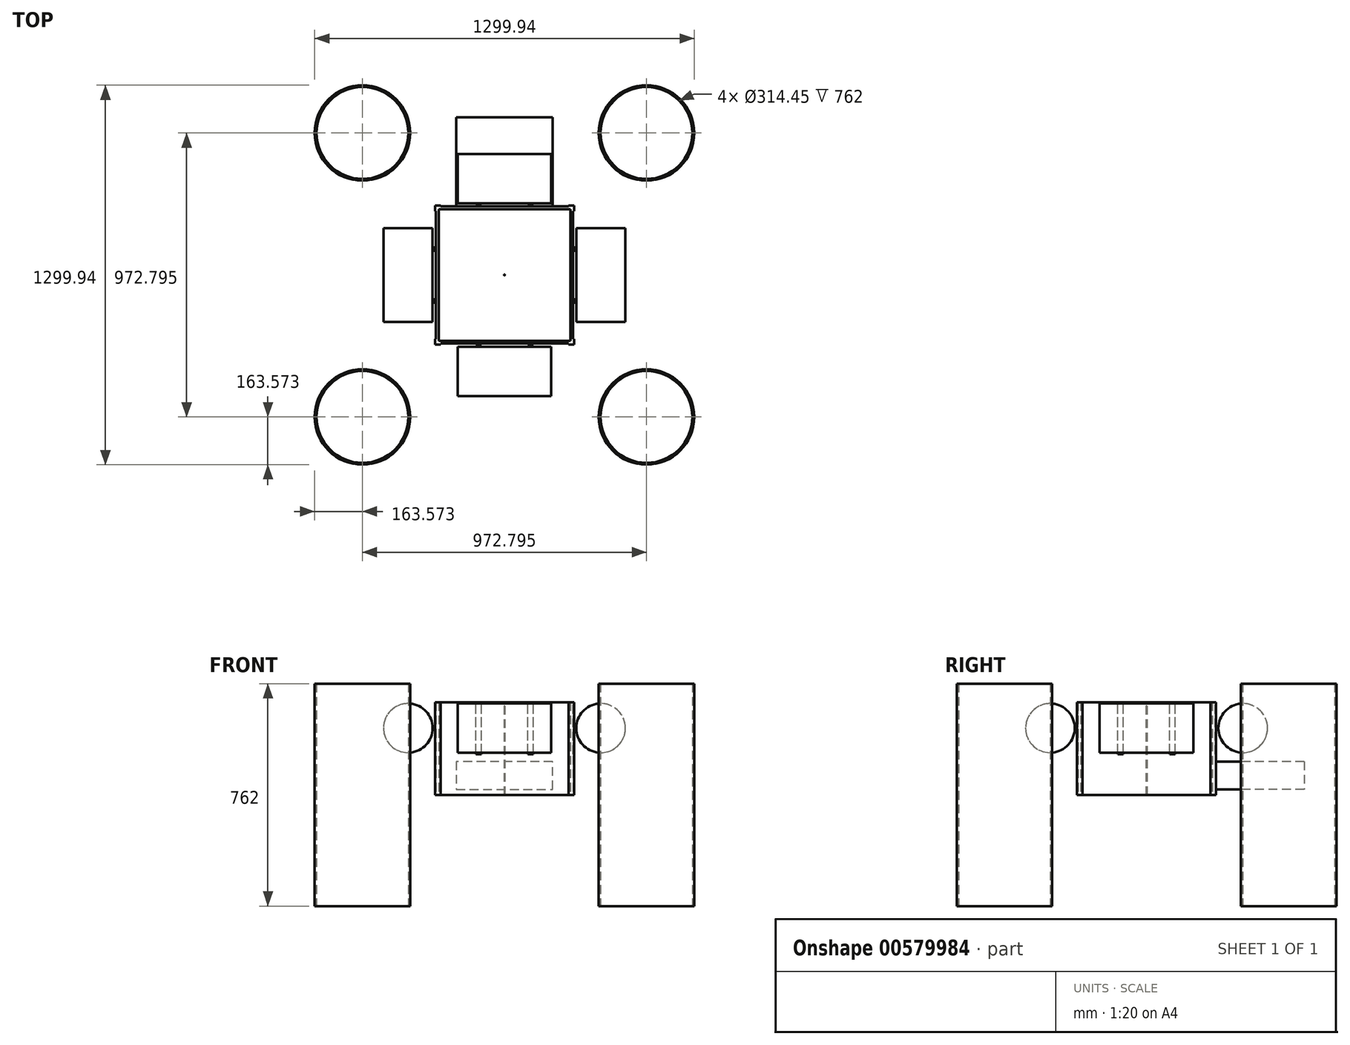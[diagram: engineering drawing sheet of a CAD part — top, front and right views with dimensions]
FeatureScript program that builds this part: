
annotation { "Feature Type Name" : "Feature", "Feature Type Description" : "" }
export const myFeature = defineFeature(function(context is Context, id is Id, definition is map)
    precondition{}
    {
        {
            var Q0;
            Q0=qCreatedBy(makeId("Top.planeOp"),FACE);
            var sketch = newSketch(context, id + "F0", { "sketchPlane" : qUnion([Q0])});
            skLineSegment(sketch, "E0.bottom", {"start": v(234.95, -234.95) * mm, "end": v(-234.95, -234.95) * mm});
            skLineSegment(sketch, "E0.top", {"start": v(234.95, 234.95) * mm, "end": v(-234.95, 234.95) * mm});
            skLineSegment(sketch, "E0.left", {"start": v(234.95, -234.95) * mm, "end": v(234.95, 234.95) * mm});
            skLineSegment(sketch, "E0.right", {"start": v(-234.95, -234.95) * mm, "end": v(-234.95, 234.95) * mm});
            skPoint(sketch, "E0.middle", {"position": v(0, 0) * mm});
            skLineSegment(sketch, "E1", {"start": v(-234.95, 238.13) * mm, "end": v(-238.13, 238.13) * mm});
            skLineSegment(sketch, "E2.bottom", {"start": v(-238.13, 238.13) * mm, "end": v(-219.08, 238.13) * mm});
            skLineSegment(sketch, "E2.top", {"start": v(-234.95, 234.95) * mm, "end": v(-219.08, 234.95) * mm});
            skLineSegment(sketch, "E2.left", {"start": v(-238.13, 238.13) * mm, "end": v(-238.13, 234.95) * mm});
            skLineSegment(sketch, "E2.right", {"start": v(-219.08, 238.13) * mm, "end": v(-219.08, 234.95) * mm});
            skLineSegment(sketch, "E3.bottom", {"start": v(-238.13, 238.13) * mm, "end": v(-234.95, 238.13) * mm});
            skLineSegment(sketch, "E3.top", {"start": v(-238.13, 219.08) * mm, "end": v(-234.95, 219.08) * mm});
            skLineSegment(sketch, "E3.left", {"start": v(-238.13, 238.13) * mm, "end": v(-238.13, 219.08) * mm});
            skLineSegment(sketch, "E3.right", {"start": v(-234.95, 234.95) * mm, "end": v(-234.95, 219.08) * mm});
            skLineSegment(sketch, "E4.1.0", {"start": v(-234.95, -234.95) * mm, "end": v(-219.08, -234.95) * mm});
            skLineSegment(sketch, "E4.1.1", {"start": v(-238.13, -238.13) * mm, "end": v(-219.08, -238.13) * mm});
            skLineSegment(sketch, "E4.1.2", {"start": v(-238.13, -238.13) * mm, "end": v(-238.13, -219.08) * mm});
            skLineSegment(sketch, "E4.1.3", {"start": v(-234.95, -234.95) * mm, "end": v(-234.95, -219.08) * mm});
            skLineSegment(sketch, "E4.1.4", {"start": v(-238.13, -219.08) * mm, "end": v(-234.95, -219.08) * mm});
            skLineSegment(sketch, "E4.1.5", {"start": v(-219.08, -238.13) * mm, "end": v(-219.08, -234.95) * mm});
            skLineSegment(sketch, "E4.1.6", {"start": v(-238.13, -238.13) * mm, "end": v(-234.95, -238.13) * mm});
            skLineSegment(sketch, "E4.1.7", {"start": v(-238.13, -238.13) * mm, "end": v(-238.13, -234.95) * mm});
            skLineSegment(sketch, "E4.1.8", {"start": v(-238.13, -234.95) * mm, "end": v(-238.13, -238.13) * mm});
            skLineSegment(sketch, "E4.2.0", {"start": v(234.95, -234.95) * mm, "end": v(234.95, -219.08) * mm});
            skLineSegment(sketch, "E4.2.1", {"start": v(238.13, -238.13) * mm, "end": v(238.13, -219.08) * mm});
            skLineSegment(sketch, "E4.2.2", {"start": v(238.13, -238.13) * mm, "end": v(219.08, -238.13) * mm});
            skLineSegment(sketch, "E4.2.3", {"start": v(234.95, -234.95) * mm, "end": v(219.08, -234.95) * mm});
            skLineSegment(sketch, "E4.2.4", {"start": v(219.08, -238.13) * mm, "end": v(219.08, -234.95) * mm});
            skLineSegment(sketch, "E4.2.5", {"start": v(238.13, -219.08) * mm, "end": v(234.95, -219.08) * mm});
            skLineSegment(sketch, "E4.2.6", {"start": v(238.13, -238.13) * mm, "end": v(238.13, -234.95) * mm});
            skLineSegment(sketch, "E4.2.7", {"start": v(238.13, -238.13) * mm, "end": v(234.95, -238.13) * mm});
            skLineSegment(sketch, "E4.2.8", {"start": v(234.95, -238.13) * mm, "end": v(238.13, -238.13) * mm});
            skLineSegment(sketch, "E4.3.0", {"start": v(234.95, 234.95) * mm, "end": v(219.08, 234.95) * mm});
            skLineSegment(sketch, "E4.3.1", {"start": v(238.13, 238.13) * mm, "end": v(219.08, 238.13) * mm});
            skLineSegment(sketch, "E4.3.2", {"start": v(238.13, 238.13) * mm, "end": v(238.13, 219.08) * mm});
            skLineSegment(sketch, "E4.3.3", {"start": v(234.95, 234.95) * mm, "end": v(234.95, 219.08) * mm});
            skLineSegment(sketch, "E4.3.4", {"start": v(238.13, 219.08) * mm, "end": v(234.95, 219.08) * mm});
            skLineSegment(sketch, "E4.3.5", {"start": v(219.08, 238.13) * mm, "end": v(219.08, 234.95) * mm});
            skLineSegment(sketch, "E4.3.6", {"start": v(238.13, 238.13) * mm, "end": v(234.95, 238.13) * mm});
            skLineSegment(sketch, "E4.3.7", {"start": v(238.13, 238.13) * mm, "end": v(238.13, 234.95) * mm});
            skLineSegment(sketch, "E4.3.8", {"start": v(238.13, 234.95) * mm, "end": v(238.13, 238.13) * mm});
            skLineSegment(sketch, "E5.0", {"start": v(225.43, 225.43) * mm, "end": v(-225.42, 225.42) * mm});
            skLineSegment(sketch, "E5.1", {"start": v(225.43, -225.42) * mm, "end": v(225.43, 225.42) * mm});
            skLineSegment(sketch, "E5.2", {"start": v(225.43, -225.42) * mm, "end": v(-225.42, -225.43) * mm});
            skLineSegment(sketch, "E5.3", {"start": v(-225.42, -225.43) * mm, "end": v(-225.42, 225.42) * mm});
            skSolve(sketch);
        }
        {
            var Q0;
            Q0=qSketchRegion(id+"F0",true);
            extrude(context, id + "F1", {"entities" : qUnion([Q0]), "depth" : 317.5 * mm, "offsetDistance" : 25.4 * mm});
        }
        {
            var Q0;
            Q0=qCreatedBy(makeId("Right.planeOp"),FACE);
            var sketch = newSketch(context, id + "F2", { "sketchPlane" : qUnion([Q0])});
            skLineSegment(sketch, "E6", {"start": v(234.95, 0) * mm, "end": v(234.95, 228.6) * mm});
            skLineSegment(sketch, "E7", {"start": v(234.95, 228.6) * mm, "end": v(330.2, 228.6) * mm});
            skCircle(sketch, "E8", {"center": v(330.2, 228.6) * mm, "radius": 84.14 * mm});
            skSolve(sketch);
        }
        {
            var Q0;
            Q0=qSketchRegion(id+"F2",true);
            extrude(context, id + "F3", {"entities" : qUnion([Q0]), "endBound" : BoundingType.SYMMETRIC, "depth" : 320.67 * mm, "offsetDistance" : 25.4 * mm});
        }
        {
            var Q0;
            Q0=makeQuery(id+"F1.opExtrude","CAP_FACE",FACE,{"disambiguationData":[OSD([sQuery(id+"F0.wireOp",EDGE,"E0.bottom"),sQuery(id+"F0.wireOp",EDGE,"E0.top"),sQuery(id+"F0.wireOp",EDGE,"E0.left"),sQuery(id+"F0.wireOp",EDGE,"E0.right"),sQuery(id+"F0.wireOp",EDGE,"E2.bottom"),sQuery(id+"F0.wireOp",EDGE,"E2.right"),sQuery(id+"F0.wireOp",EDGE,"E3.bottom"),sQuery(id+"F0.wireOp",EDGE,"E3.top"),sQuery(id+"F0.wireOp",EDGE,"E3.left"),sQuery(id+"F0.wireOp",EDGE,"E4.1.1"),sQuery(id+"F0.wireOp",EDGE,"E4.1.2"),sQuery(id+"F0.wireOp",EDGE,"E4.1.4"),sQuery(id+"F0.wireOp",EDGE,"E4.1.5"),sQuery(id+"F0.wireOp",EDGE,"E4.1.6"),sQuery(id+"F0.wireOp",EDGE,"E4.1.8"),sQuery(id+"F0.wireOp",EDGE,"E4.2.1"),sQuery(id+"F0.wireOp",EDGE,"E4.2.2"),sQuery(id+"F0.wireOp",EDGE,"E4.2.4"),sQuery(id+"F0.wireOp",EDGE,"E4.2.5"),sQuery(id+"F0.wireOp",EDGE,"E4.2.6"),sQuery(id+"F0.wireOp",EDGE,"E4.2.8"),sQuery(id+"F0.wireOp",EDGE,"E4.3.1"),sQuery(id+"F0.wireOp",EDGE,"E4.3.2"),sQuery(id+"F0.wireOp",EDGE,"E4.3.4"),sQuery(id+"F0.wireOp",EDGE,"E4.3.5"),sQuery(id+"F0.wireOp",EDGE,"E4.3.6"),sQuery(id+"F0.wireOp",EDGE,"E4.3.8"),sQuery(id+"F0.wireOp",EDGE,"E5.0"),sQuery(id+"F0.wireOp",EDGE,"E5.1"),sQuery(id+"F0.wireOp",EDGE,"E5.2"),sQuery(id+"F0.wireOp",EDGE,"E5.3")])],"isStart":false});
            var sketch = newSketch(context, id + "F4", { "sketchPlane" : qUnion([Q0])});
            skLineSegment(sketch, "E9", {"start": v(0, 234.95) * mm, "end": v(-79.38, 234.95) * mm});
            skLineSegment(sketch, "E10", {"start": v(-79.38, 234.95) * mm, "end": v(-79.38, 238.12) * mm});
            skLineSegment(sketch, "E11", {"start": v(-79.38, 238.12) * mm, "end": v(-98.43, 238.12) * mm});
            skLineSegment(sketch, "E12", {"start": v(-98.43, 238.12) * mm, "end": v(-98.43, 234.95) * mm});
            skLineSegment(sketch, "E13", {"start": v(-98.43, 234.95) * mm, "end": v(-79.38, 234.95) * mm});
            skLineSegment(sketch, "E14", {"start": v(0, 234.95) * mm, "end": v(0, 171.04) * mm});
            skPoint(sketch, "E14.endSnap0", {"position": v(0, 225.42) * mm});
            skLineSegment(sketch, "E15.MirrorCS", {"start": v(79.37, 234.95) * mm, "end": v(79.37, 238.12) * mm});
            skLineSegment(sketch, "E16.MirrorCS", {"start": v(98.43, 238.12) * mm, "end": v(98.43, 234.95) * mm});
            skLineSegment(sketch, "E17.MirrorCS", {"start": v(0, 234.95) * mm, "end": v(79.38, 234.95) * mm});
            skLineSegment(sketch, "E18.MirrorCS", {"start": v(79.38, 238.13) * mm, "end": v(98.43, 238.13) * mm});
            skLineSegment(sketch, "E19.MirrorCS", {"start": v(98.43, 234.95) * mm, "end": v(79.38, 234.95) * mm});
            skSolve(sketch);
        }
        {
            var Q0;
            Q0=qSketchRegion(id+"F4",true);
            extrude(context, id + "F5", {"entities" : qUnion([Q0]), "oppositeDirection" : true, "depth" : 177.8 * mm, "offsetDistance" : 25.4 * mm});
        }
        {
            var Q0;
            Q0=qCreatedBy(makeId("Top.planeOp"),FACE);
            var sketch = newSketch(context, id + "F6", { "sketchPlane" : qUnion([Q0])});
            skCircle(sketch, "E20", {"center": v(0, 0) * mm, "radius": 1.59 * mm});
            skSolve(sketch);
        }
        {
            var Q0;
            Q0=qSketchRegion(id+"F6",true);
            extrude(context, id + "F7", {"entities" : qUnion([Q0]), "depth" : 304.8 * mm, "offsetDistance" : 25.4 * mm});
        }
        {
            var Q0;
            Q0=makeQuery(id+"F3.opExtrude","SWEPT_BODY",BODY,{"disambiguationData":[OSD([sQuery(id+"F2.wireOp",EDGE,"E8")])]});
            var Q1;
            Q1=makeQuery(id+"F5.opExtrude","SWEPT_BODY",BODY,{"disambiguationData":[OSD([sQuery(id+"F4.wireOp",EDGE,"E10"),sQuery(id+"F4.wireOp",EDGE,"E11"),sQuery(id+"F4.wireOp",EDGE,"E12"),sQuery(id+"F4.wireOp",EDGE,"E13")])]});
            var Q2;
            Q2=makeQuery(id+"F5.opExtrude","SWEPT_BODY",BODY,{"disambiguationData":[OSD([sQuery(id+"F4.wireOp",EDGE,"E15.MirrorCS"),sQuery(id+"F4.wireOp",EDGE,"E16.MirrorCS"),sQuery(id+"F4.wireOp",EDGE,"E18.MirrorCS"),sQuery(id+"F4.wireOp",EDGE,"E19.MirrorCS")])]});
            var Q3;
            Q3=makeQuery(id+"F7.opExtrude","SWEPT_FACE",FACE,{"disambiguationData":[OSD([sQuery(id+"F6.wireOp",EDGE,"E20")])]});
            circularPattern(context, id + "F8", {"entities" : qUnion([Q0, Q1, Q2]), "axis" : qUnion([Q3]), "angle" : 360 * degree, "instanceCount" : 4, "equalSpace" : true});
        }
        {
            var Q0;
            Q0=makeQuery(id+"F1.opExtrude","SWEPT_FACE",FACE,{"disambiguationData":[OSD([sQuery(id+"F0.wireOp",EDGE,"E0.top")])]});
            var sketch = newSketch(context, id + "F9", { "sketchPlane" : qUnion([Q0])});
            skLineSegment(sketch, "E21", {"start": v(0, 0) * mm, "end": v(0, 19.05) * mm});
            skPoint(sketch, "E21.endSnap0", {"position": v(0, 0) * mm});
            skLineSegment(sketch, "E22", {"start": v(0, 19.05) * mm, "end": v(165.1, 19.05) * mm});
            skLineSegment(sketch, "E23.MirrorCS", {"start": v(0, 19.05) * mm, "end": v(-165.1, 19.05) * mm});
            skLineSegment(sketch, "E24", {"start": v(-165.1, 19.05) * mm, "end": v(-165.1, 114.3) * mm});
            skLineSegment(sketch, "E25", {"start": v(-165.1, 114.3) * mm, "end": v(165.1, 114.3) * mm});
            skLineSegment(sketch, "E26", {"start": v(165.1, 114.3) * mm, "end": v(165.1, 19.05) * mm});
            skSolve(sketch);
        }
        {
            var Q0;
            Q0=qSketchRegion(id+"F9",true);
            extrude(context, id + "F10", {"entities" : qUnion([Q0]), "depth" : 304.8 * mm, "offsetDistance" : 25.4 * mm});
        }
        {
            var Q0;
            Q0=makeQuery(id+"F1.opExtrude","SWEPT_FACE",FACE,{"disambiguationData":[OSD([sQuery(id+"F0.wireOp",EDGE,"E4.3.2"),sQuery(id+"F0.wireOp",EDGE,"E4.3.8")])]});
            var sketch = newSketch(context, id + "F11", { "sketchPlane" : qUnion([Q0])});
            skLineSegment(sketch, "E27", {"start": v(644.53, 0) * mm, "end": v(644.53, 25.4) * mm});
            skLineSegment(sketch, "E28", {"start": v(238.13, 317.5) * mm, "end": v(314.33, 317.5) * mm});
            skArc(sketch, "E29", {"start": v(640.07, 52.43) * mm, "mid": v(524.3, 242.86) * mm, "end": v(314.33, 317.5) * mm});
            skLineSegment(sketch, "E30", {"start": v(238.13, 0) * mm, "end": v(238.13, -1.27) * mm});
            skLineSegment(sketch, "E31", {"start": v(238.13, -1.27) * mm, "end": v(219.08, -1.27) * mm});
            skArc(sketch, "E32", {"start": v(238.12, -1.27) * mm, "mid": v(428.57, 4.57) * mm, "end": v(618.3, 22.06) * mm});
            skLineSegment(sketch, "E33", {"start": v(219.08, -1.27) * mm, "end": v(219.08, 0) * mm});
            skLineSegment(sketch, "E34", {"start": v(219.08, 0) * mm, "end": v(238.13, 0) * mm});
            skLineSegment(sketch, "E35", {"start": v(238.13, 317.5) * mm, "end": v(238.13, 292.1) * mm});
            skLineSegment(sketch, "E36", {"start": v(238.13, 317.5) * mm, "end": v(263.53, 317.5) * mm});
            skLineSegment(sketch, "E37", {"start": v(238.13, 292.1) * mm, "end": v(238.13, 266.7) * mm});
            skPoint(sketch, "E38.visualSharp", {"position": v(644.52, 25.4) * mm});
            skArc(sketch, "E38.filletArc", {"start": v(618.3, 22.06) * mm, "mid": v(635.84, 32.47) * mm, "end": v(640.07, 52.43) * mm});
            skArc(sketch, "E39.0", {"start": v(238.12, 0) * mm, "mid": v(428.5, 5.83) * mm, "end": v(618.15, 23.32) * mm});
            skArc(sketch, "E39.1", {"start": v(618.15, 23.32) * mm, "mid": v(634.81, 33.21) * mm, "end": v(638.82, 52.17) * mm});
            skArc(sketch, "E39.2", {"start": v(638.82, 52.17) * mm, "mid": v(523.5, 241.87) * mm, "end": v(314.33, 316.23) * mm});
            skLineSegment(sketch, "E39.3", {"start": v(238.13, 316.23) * mm, "end": v(314.33, 316.23) * mm});
            skLineSegment(sketch, "E40", {"start": v(263.53, 317.5) * mm, "end": v(263.53, 316.23) * mm});
            skArc(sketch, "E41", {"start": v(263.53, 316.23) * mm, "mid": v(245.65, 309.62) * mm, "end": v(238.13, 292.1) * mm});
            skLineSegment(sketch, "E42", {"start": v(263.53, 316.23) * mm, "end": v(288.93, 316.23) * mm});
            skLineSegment(sketch, "E43.0", {"start": v(263.5, 314.96) * mm, "end": v(288.93, 314.96) * mm});
            skArc(sketch, "E43.1", {"start": v(263.5, 314.96) * mm, "mid": v(246.53, 308.7) * mm, "end": v(239.4, 292.1) * mm});
            skLineSegment(sketch, "E43.2", {"start": v(239.4, 292.1) * mm, "end": v(239.4, 266.7) * mm});
            skLineSegment(sketch, "E44", {"start": v(288.93, 314.96) * mm, "end": v(288.93, 316.23) * mm});
            skLineSegment(sketch, "E45", {"start": v(238.13, 266.7) * mm, "end": v(239.4, 266.7) * mm});
            skLineSegment(sketch, "E46", {"start": v(238.13, 317.5) * mm, "end": v(234.95, 317.5) * mm});
            skLineSegment(sketch, "E47", {"start": v(234.95, 317.5) * mm, "end": v(234.95, 316.23) * mm});
            skLineSegment(sketch, "E48", {"start": v(234.95, 316.23) * mm, "end": v(238.13, 316.23) * mm});
            skSolve(sketch);
        }
        {
            var Q0;
            Q0=qSketchRegion(id+"F11",true);
            extrude(context, id + "F12", {"entities" : qUnion([Q0]), "oppositeDirection" : true, "depth" : 679.45 * mm, "offsetDistance" : 25.4 * mm, "hasSecondDirection" : true, "secondDirectionOppositeDirection" : false, "secondDirectionDepth" : 203.2 * mm});
        }
        {
            var Q0;
            Q0=qCreatedBy(makeId("Top.planeOp"),FACE);
            var sketch = newSketch(context, id + "F13", { "sketchPlane" : qUnion([Q0])});
            skLineSegment(sketch, "E49", {"start": v(0, 0) * mm, "end": v(0, 486.4) * mm});
            skLineSegment(sketch, "E50", {"start": v(0, 486.4) * mm, "end": v(486.4, 486.4) * mm});
            skCircle(sketch, "E51", {"center": v(486.4, 486.4) * mm, "radius": 157.23 * mm});
            skCircle(sketch, "E52.0", {"center": v(486.4, 486.4) * mm, "radius": 163.58 * mm});
            skCircle(sketch, "E53.1.0", {"center": v(-486.4, 486.4) * mm, "radius": 163.58 * mm});
            skCircle(sketch, "E53.1.1", {"center": v(-486.4, 486.4) * mm, "radius": 157.23 * mm});
            skCircle(sketch, "E53.2.0", {"center": v(-486.4, -486.4) * mm, "radius": 163.58 * mm});
            skCircle(sketch, "E53.2.1", {"center": v(-486.4, -486.4) * mm, "radius": 157.23 * mm});
            skCircle(sketch, "E53.3.0", {"center": v(486.4, -486.4) * mm, "radius": 163.58 * mm});
            skCircle(sketch, "E53.3.1", {"center": v(486.4, -486.4) * mm, "radius": 157.23 * mm});
            skPoint(sketch, "E53.center", {"position": v(0, 0) * mm});
            skSolve(sketch);
        }
        {
            var Q0;
            Q0=qSketchRegion(id+"F13",true);
            extrude(context, id + "F14", {"entities" : qUnion([Q0]), "endBound" : BoundingType.SYMMETRIC, "depth" : 762 * mm, "offsetDistance" : 25.4 * mm});
        }
        {
            var Q0;
            Q0=makeQuery(id+"F14.opExtrude","SWEPT_BODY",BODY,{"disambiguationData":[OSD([sQuery(id+"F13.wireOp",EDGE,"E51"),sQuery(id+"F13.wireOp",EDGE,"E52.0")])]});
            var Q1;
            Q1=makeQuery(id+"F14.opExtrude","SWEPT_BODY",BODY,{"disambiguationData":[OSD([sQuery(id+"F13.wireOp",EDGE,"E53.1.0"),sQuery(id+"F13.wireOp",EDGE,"E53.1.1")])]});
            var Q2;
            Q2=makeQuery(id+"F12.opExtrude","SWEPT_BODY",BODY,{"disambiguationData":[OSD([sQuery(id+"F11.wireOp",EDGE,"E28"),sQuery(id+"F11.wireOp",EDGE,"E29"),sQuery(id+"F11.wireOp",EDGE,"E31"),sQuery(id+"F11.wireOp",EDGE,"E32"),sQuery(id+"F11.wireOp",EDGE,"E33"),sQuery(id+"F11.wireOp",EDGE,"E34"),sQuery(id+"F11.wireOp",EDGE,"E35"),sQuery(id+"F11.wireOp",EDGE,"E36"),sQuery(id+"F11.wireOp",EDGE,"E37"),sQuery(id+"F11.wireOp",EDGE,"E38.filletArc"),sQuery(id+"F11.wireOp",EDGE,"E39.0"),sQuery(id+"F11.wireOp",EDGE,"E39.1"),sQuery(id+"F11.wireOp",EDGE,"E39.2"),sQuery(id+"F11.wireOp",EDGE,"E39.3"),sQuery(id+"F11.wireOp",EDGE,"E41"),sQuery(id+"F11.wireOp",EDGE,"E43.0"),sQuery(id+"F11.wireOp",EDGE,"E43.1"),sQuery(id+"F11.wireOp",EDGE,"E43.2"),sQuery(id+"F11.wireOp",EDGE,"E44"),sQuery(id+"F11.wireOp",EDGE,"E45"),sQuery(id+"F11.wireOp",EDGE,"E46"),sQuery(id+"F11.wireOp",EDGE,"E47"),sQuery(id+"F11.wireOp",EDGE,"E48")])]});
            booleanBodies(context, id + "F15", {"operationType" : BooleanOperationType.SUBTRACTION, "tools" : qUnion([Q0, Q1]), "targets" : qUnion([Q2]), "keepTools" : true});
        }
        {
            var Q0;
            Q0=makeQuery(id+"F15.opBoolean","SPLIT",BODY,{"disambiguationData":[OD(1.0)],"derivedFrom":makeQuery(id+"F12.opExtrude","SWEPT_BODY",BODY,{"disambiguationData":[OSD([sQuery(id+"F11.wireOp",EDGE,"E28"),sQuery(id+"F11.wireOp",EDGE,"E29"),sQuery(id+"F11.wireOp",EDGE,"E31"),sQuery(id+"F11.wireOp",EDGE,"E32"),sQuery(id+"F11.wireOp",EDGE,"E33"),sQuery(id+"F11.wireOp",EDGE,"E34"),sQuery(id+"F11.wireOp",EDGE,"E35"),sQuery(id+"F11.wireOp",EDGE,"E36"),sQuery(id+"F11.wireOp",EDGE,"E37"),sQuery(id+"F11.wireOp",EDGE,"E38.filletArc"),sQuery(id+"F11.wireOp",EDGE,"E39.0"),sQuery(id+"F11.wireOp",EDGE,"E39.1"),sQuery(id+"F11.wireOp",EDGE,"E39.2"),sQuery(id+"F11.wireOp",EDGE,"E39.3"),sQuery(id+"F11.wireOp",EDGE,"E41"),sQuery(id+"F11.wireOp",EDGE,"E43.0"),sQuery(id+"F11.wireOp",EDGE,"E43.1"),sQuery(id+"F11.wireOp",EDGE,"E43.2"),sQuery(id+"F11.wireOp",EDGE,"E44"),sQuery(id+"F11.wireOp",EDGE,"E45"),sQuery(id+"F11.wireOp",EDGE,"E46"),sQuery(id+"F11.wireOp",EDGE,"E47"),sQuery(id+"F11.wireOp",EDGE,"E48")])]})});
            var Q1;
            Q1=makeQuery(id+"F15.opBoolean","SPLIT",BODY,{"disambiguationData":[OD(2.0)],"derivedFrom":makeQuery(id+"F12.opExtrude","SWEPT_BODY",BODY,{"disambiguationData":[OSD([sQuery(id+"F11.wireOp",EDGE,"E28"),sQuery(id+"F11.wireOp",EDGE,"E29"),sQuery(id+"F11.wireOp",EDGE,"E31"),sQuery(id+"F11.wireOp",EDGE,"E32"),sQuery(id+"F11.wireOp",EDGE,"E33"),sQuery(id+"F11.wireOp",EDGE,"E34"),sQuery(id+"F11.wireOp",EDGE,"E35"),sQuery(id+"F11.wireOp",EDGE,"E36"),sQuery(id+"F11.wireOp",EDGE,"E37"),sQuery(id+"F11.wireOp",EDGE,"E38.filletArc"),sQuery(id+"F11.wireOp",EDGE,"E39.0"),sQuery(id+"F11.wireOp",EDGE,"E39.1"),sQuery(id+"F11.wireOp",EDGE,"E39.2"),sQuery(id+"F11.wireOp",EDGE,"E39.3"),sQuery(id+"F11.wireOp",EDGE,"E41"),sQuery(id+"F11.wireOp",EDGE,"E43.0"),sQuery(id+"F11.wireOp",EDGE,"E43.1"),sQuery(id+"F11.wireOp",EDGE,"E43.2"),sQuery(id+"F11.wireOp",EDGE,"E44"),sQuery(id+"F11.wireOp",EDGE,"E45"),sQuery(id+"F11.wireOp",EDGE,"E46"),sQuery(id+"F11.wireOp",EDGE,"E47"),sQuery(id+"F11.wireOp",EDGE,"E48")])]})});
            var Q2;
            Q2=makeQuery(id+"F15.opBoolean","SPLIT",BODY,{"disambiguationData":[OD(4.0)],"derivedFrom":makeQuery(id+"F12.opExtrude","SWEPT_BODY",BODY,{"disambiguationData":[OSD([sQuery(id+"F11.wireOp",EDGE,"E28"),sQuery(id+"F11.wireOp",EDGE,"E29"),sQuery(id+"F11.wireOp",EDGE,"E31"),sQuery(id+"F11.wireOp",EDGE,"E32"),sQuery(id+"F11.wireOp",EDGE,"E33"),sQuery(id+"F11.wireOp",EDGE,"E34"),sQuery(id+"F11.wireOp",EDGE,"E35"),sQuery(id+"F11.wireOp",EDGE,"E36"),sQuery(id+"F11.wireOp",EDGE,"E37"),sQuery(id+"F11.wireOp",EDGE,"E38.filletArc"),sQuery(id+"F11.wireOp",EDGE,"E39.0"),sQuery(id+"F11.wireOp",EDGE,"E39.1"),sQuery(id+"F11.wireOp",EDGE,"E39.2"),sQuery(id+"F11.wireOp",EDGE,"E39.3"),sQuery(id+"F11.wireOp",EDGE,"E41"),sQuery(id+"F11.wireOp",EDGE,"E43.0"),sQuery(id+"F11.wireOp",EDGE,"E43.1"),sQuery(id+"F11.wireOp",EDGE,"E43.2"),sQuery(id+"F11.wireOp",EDGE,"E44"),sQuery(id+"F11.wireOp",EDGE,"E45"),sQuery(id+"F11.wireOp",EDGE,"E46"),sQuery(id+"F11.wireOp",EDGE,"E47"),sQuery(id+"F11.wireOp",EDGE,"E48")])]})});
            var Q3;
            Q3=makeQuery(id+"F15.opBoolean","SPLIT",BODY,{"disambiguationData":[OD(3.0)],"derivedFrom":makeQuery(id+"F12.opExtrude","SWEPT_BODY",BODY,{"disambiguationData":[OSD([sQuery(id+"F11.wireOp",EDGE,"E28"),sQuery(id+"F11.wireOp",EDGE,"E29"),sQuery(id+"F11.wireOp",EDGE,"E31"),sQuery(id+"F11.wireOp",EDGE,"E32"),sQuery(id+"F11.wireOp",EDGE,"E33"),sQuery(id+"F11.wireOp",EDGE,"E34"),sQuery(id+"F11.wireOp",EDGE,"E35"),sQuery(id+"F11.wireOp",EDGE,"E36"),sQuery(id+"F11.wireOp",EDGE,"E37"),sQuery(id+"F11.wireOp",EDGE,"E38.filletArc"),sQuery(id+"F11.wireOp",EDGE,"E39.0"),sQuery(id+"F11.wireOp",EDGE,"E39.1"),sQuery(id+"F11.wireOp",EDGE,"E39.2"),sQuery(id+"F11.wireOp",EDGE,"E39.3"),sQuery(id+"F11.wireOp",EDGE,"E41"),sQuery(id+"F11.wireOp",EDGE,"E43.0"),sQuery(id+"F11.wireOp",EDGE,"E43.1"),sQuery(id+"F11.wireOp",EDGE,"E43.2"),sQuery(id+"F11.wireOp",EDGE,"E44"),sQuery(id+"F11.wireOp",EDGE,"E45"),sQuery(id+"F11.wireOp",EDGE,"E46"),sQuery(id+"F11.wireOp",EDGE,"E47"),sQuery(id+"F11.wireOp",EDGE,"E48")])]})});
            deleteBodies(context, id + "F16", {"entities" : qUnion([Q0, Q1, Q2, Q3])});
        }
    });
